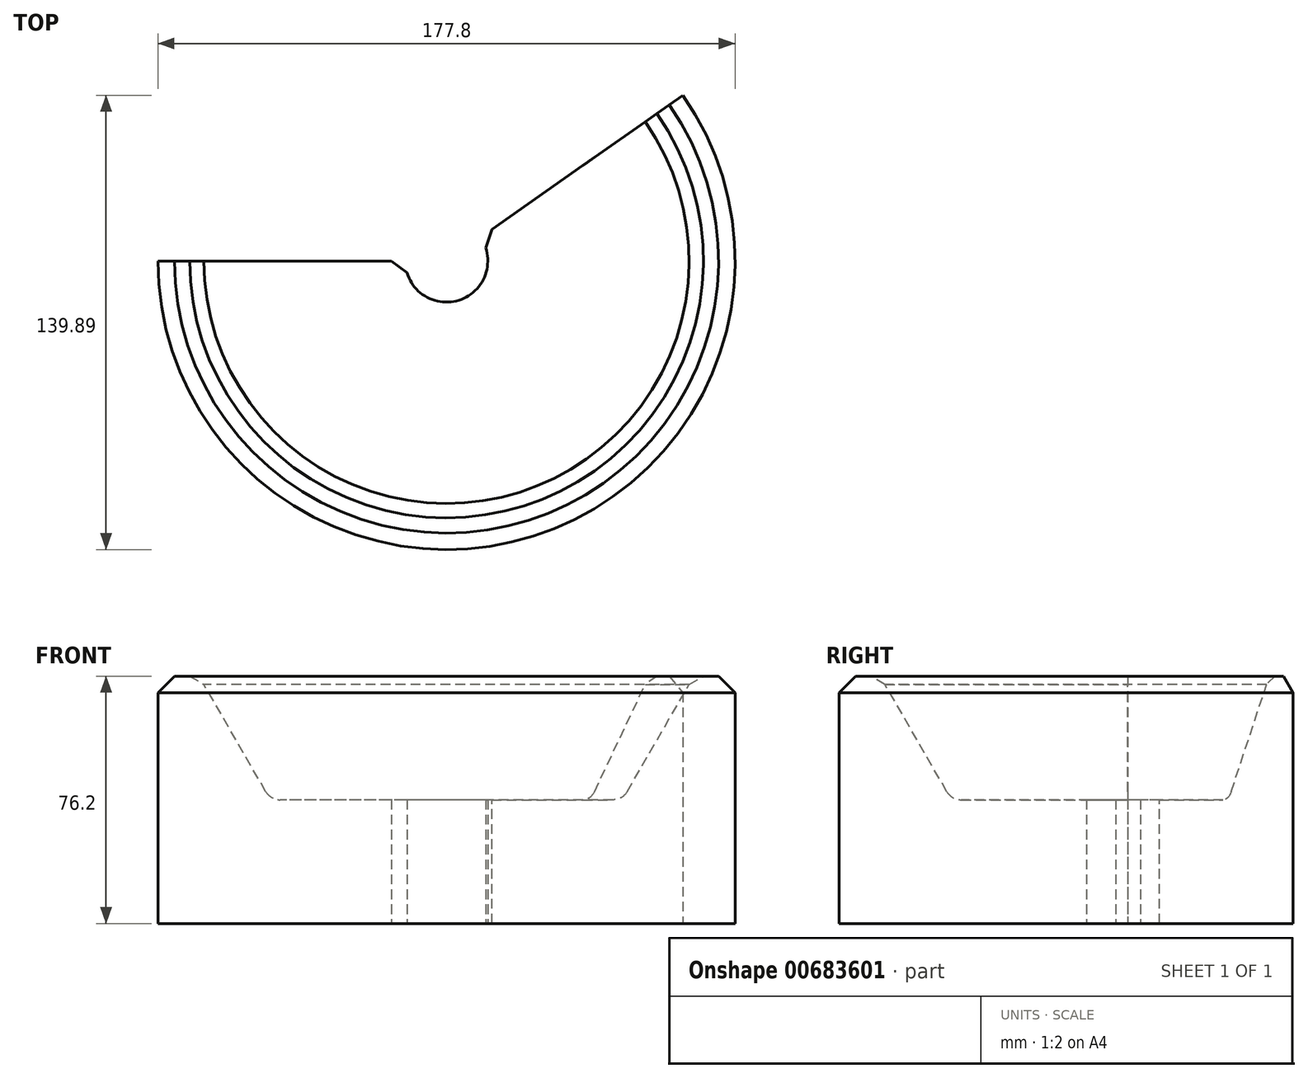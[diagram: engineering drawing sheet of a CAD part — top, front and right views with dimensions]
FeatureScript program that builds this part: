
annotation { "Feature Type Name" : "Feature", "Feature Type Description" : "" }
export const myFeature = defineFeature(function(context is Context, id is Id, definition is map)
    precondition{}
    {
        {
            var Q0;
            Q0=qCreatedBy(makeId("Front.planeOp"),FACE);
            var sketch = newSketch(context, id + "F0", { "sketchPlane" : qUnion([Q0])});
            skLineSegment(sketch, "E0", {"start": v(-12.7, 0) * mm, "end": v(-12.7, 38.1) * mm});
            skLineSegment(sketch, "E1", {"start": v(-12.7, 38.1) * mm, "end": v(-54.2, 38.1) * mm});
            skLineSegment(sketch, "E2", {"start": v(-54.2, 38.1) * mm, "end": v(-76.2, 76.2) * mm});
            skLineSegment(sketch, "E3", {"start": v(-76.2, 76.2) * mm, "end": v(-88.9, 76.2) * mm});
            skLineSegment(sketch, "E4", {"start": v(-88.9, 76.2) * mm, "end": v(-88.9, 0) * mm});
            skLineSegment(sketch, "E5", {"start": v(-88.9, 0) * mm, "end": v(-12.7, 0) * mm});
            skLineSegment(sketch, "E6", {"start": v(0, 0) * mm, "end": v(0, 18.47) * mm});
            skSolve(sketch);
        }
        {
            var Q0;
            Q0=makeQuery(id+"F0.imprint","IMPRINT",FACE,{"disambiguationData":[TD([[makeQuery(id+"F0.imprint","IMPRINT",EDGE,{"derivedFrom":sQuery(id+"F0.wireOp",EDGE,"E0")}),1.0]])]});
            var Q1;
            Q1=sQuery(id+"F0.wireOp",EDGE,"E6");
            revolve(context, id + "F1", {"entities" : qUnion([Q0]), "axis" : qUnion([Q1]), "revolveType" : RevolveType.ONE_DIRECTION, "angle" : 215 * degree, "surfaceOperationType" : NewSurfaceOperationType.NEW});
        }
        {
            var Q0;
            Q0=makeQuery(id+"F1.opRevolve","SWEPT_EDGE",EDGE,{"disambiguationData":[OSD([sQuery(id+"F0.wireOp",EDGE,"E1"),sQuery(id+"F0.wireOp",EDGE,"E2")])]});
            fillet(context, id + "F2", {"entities" : qUnion([Q0]), "radius" : 5.08 * mm, "tangentPropagation" : true, "allowEdgeOverflow" : false});
        }
        {
            var Q0;
            Q0=makeQuery(id+"F1.opRevolve","CAP_EDGE",EDGE,{"disambiguationData":[OSD([sQuery(id+"F0.wireOp",EDGE,"E0")])],"isStart":false});
            var Q1;
            Q1=makeQuery(id+"F1.opRevolve","CAP_EDGE",EDGE,{"disambiguationData":[OSD([sQuery(id+"F0.wireOp",EDGE,"E0")])],"isStart":true});
            chamfer(context, id + "F3", {"entities" : qUnion([Q0, Q1]), "width" : 5.08 * mm, "tangentPropagation" : true});
        }
        {
            var Q0;
            Q0=makeQuery(id+"F1.opRevolve","SWEPT_EDGE",EDGE,{"disambiguationData":[OSD([sQuery(id+"F0.wireOp",EDGE,"E2"),sQuery(id+"F0.wireOp",EDGE,"E3")])]});
            var Q1;
            Q1=makeQuery(id+"F1.opRevolve","SWEPT_EDGE",EDGE,{"disambiguationData":[OSD([sQuery(id+"F0.wireOp",EDGE,"E3"),sQuery(id+"F0.wireOp",EDGE,"E4")])]});
            chamfer(context, id + "F4", {"entities" : qUnion([Q0, Q1]), "width" : 5.08 * mm, "tangentPropagation" : true});
        }
    });
